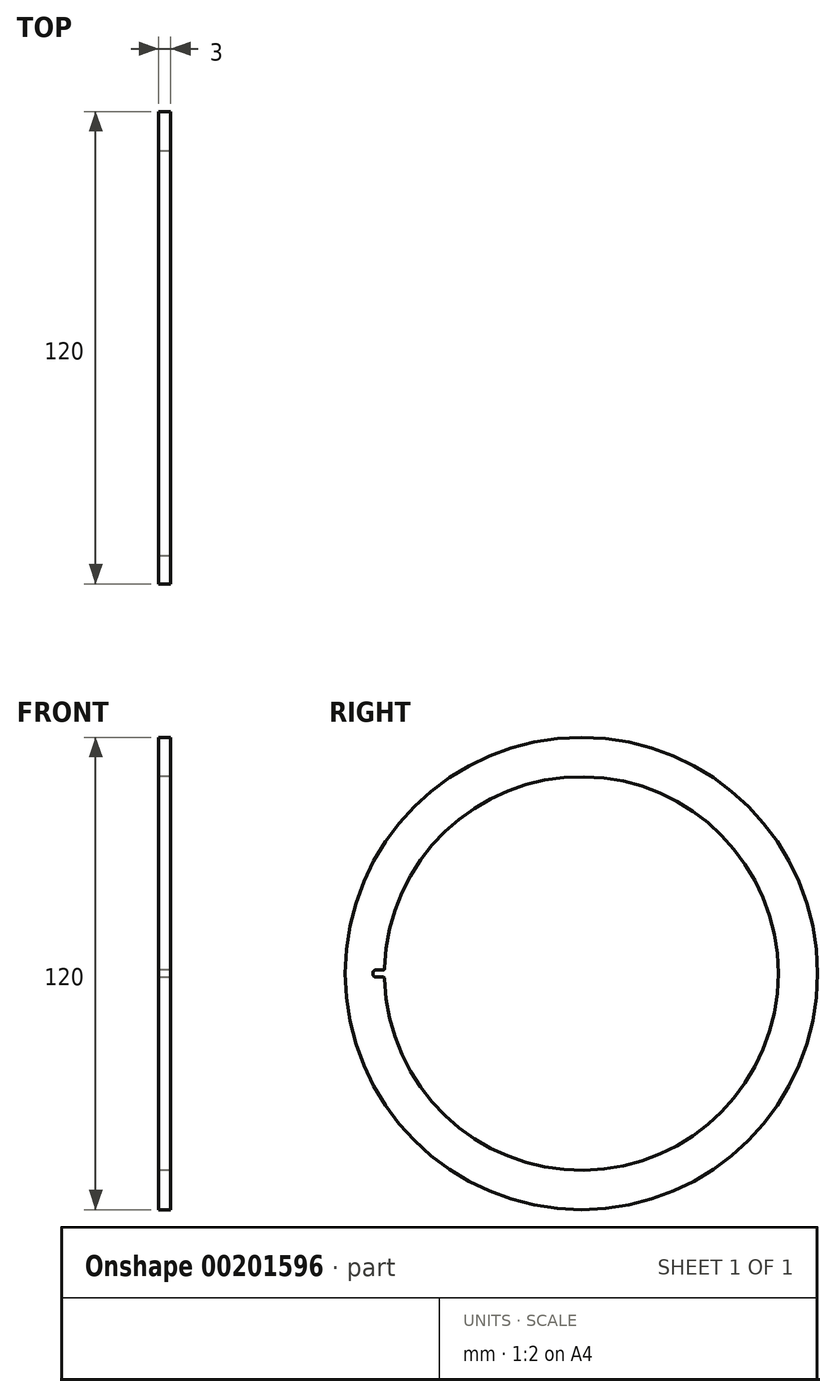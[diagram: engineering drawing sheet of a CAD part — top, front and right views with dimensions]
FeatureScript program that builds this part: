
annotation { "Feature Type Name" : "Feature", "Feature Type Description" : "" }
export const myFeature = defineFeature(function(context is Context, id is Id, definition is map)
    precondition{}
    {
        {
            var Q0;
            Q0=qCreatedBy(makeId("Top.planeOp"),FACE);
            var sketch = newSketch(context, id + "F0", { "sketchPlane" : qUnion([Q0])});
            skLineSegment(sketch, "E0.bottom", {"start": v(-60, 60) * mm, "end": v(60, 60) * mm});
            skLineSegment(sketch, "E0.top", {"start": v(-60, -60) * mm, "end": v(60, -60) * mm});
            skLineSegment(sketch, "E0.left", {"start": v(-60, 60) * mm, "end": v(-60, -60) * mm});
            skLineSegment(sketch, "E0.right", {"start": v(60, 60) * mm, "end": v(60, -60) * mm});
            skPoint(sketch, "E0.middle", {"position": v(0, 0) * mm});
            skSolve(sketch);
        }
        {
            var Q0;
            Q0=qCreatedBy(makeId("Right.planeOp"),FACE);
            var sketch = newSketch(context, id + "F1", { "sketchPlane" : qUnion([Q0])});
            skCircle(sketch, "E1", {"center": v(0, 0) * mm, "radius": 60 * mm});
            skCircle(sketch, "E2", {"center": v(0, 0) * mm, "radius": 50 * mm});
            skLineSegment(sketch, "E3", {"start": v(0, 0) * mm, "end": v(-59.98, 1.57) * mm, "construction": true});
            skLineSegment(sketch, "E4", {"start": v(0, 0) * mm, "end": v(-59.98, -1.57) * mm, "construction": true});
            skLineSegment(sketch, "E5", {"start": v(0, 0) * mm, "end": v(-60, 1.05) * mm, "construction": true});
            skLineSegment(sketch, "E6", {"start": v(0, 0) * mm, "end": v(-60, -1.05) * mm, "construction": true});
            skLineSegment(sketch, "E7.bottom", {"start": v(-50, 0.87) * mm, "end": v(-52.24, 0.87) * mm});
            skLineSegment(sketch, "E7.top", {"start": v(-50, -0.87) * mm, "end": v(-52.24, -0.87) * mm});
            skLineSegment(sketch, "E7.left", {"start": v(-50, 0.87) * mm, "end": v(-50, -0.87) * mm});
            skLineSegment(sketch, "E7.right", {"start": v(-53, 0.12) * mm, "end": v(-53, -0.12) * mm});
            skPoint(sketch, "E8.visualSharp", {"position": v(-53, 0.87) * mm});
            skArc(sketch, "E8.filletArc", {"start": v(-52.24, 0.87) * mm, "mid": v(-52.77, 0.65) * mm, "end": v(-53, 0.12) * mm});
            skPoint(sketch, "E9.visualSharp", {"position": v(-53, -0.87) * mm});
            skArc(sketch, "E9.filletArc", {"start": v(-53, -0.12) * mm, "mid": v(-52.77, -0.65) * mm, "end": v(-52.24, -0.87) * mm});
            skSolve(sketch);
        }
        {
            var Q0;
            Q0=makeQuery(id+"F1.imprint","IMPRINT",FACE,{"disambiguationData":[TD([[makeQuery(id+"F1.imprint","IMPRINT",EDGE,{"derivedFrom":sQuery(id+"F1.wireOp",EDGE,"E1")}),1.0]])]});
            extrude(context, id + "F2", {"entities" : qUnion([Q0]), "depth" : 3 * mm});
        }
        {
            var Q0;
            Q0=makeQuery(id+"F2.opExtrude","SWEPT_EDGE",EDGE,{"disambiguationData":[OSD([sQuery(id+"F1.wireOp",EDGE,"E2"),sQuery(id+"F1.wireOp",EDGE,"E7.bottom"),sQuery(id+"F1.wireOp",EDGE,"E7.left")])]});
            var Q1;
            Q1=makeQuery(id+"F2.opExtrude","SWEPT_EDGE",EDGE,{"disambiguationData":[OSD([sQuery(id+"F1.wireOp",EDGE,"E2"),sQuery(id+"F1.wireOp",EDGE,"E7.top"),sQuery(id+"F1.wireOp",EDGE,"E7.left")])]});
            fillet(context, id + "F3", {"entities" : qUnion([Q0, Q1]), "radius" : .5 * mm, "tangentPropagation" : true, "allowEdgeOverflow" : false});
        }
    });
